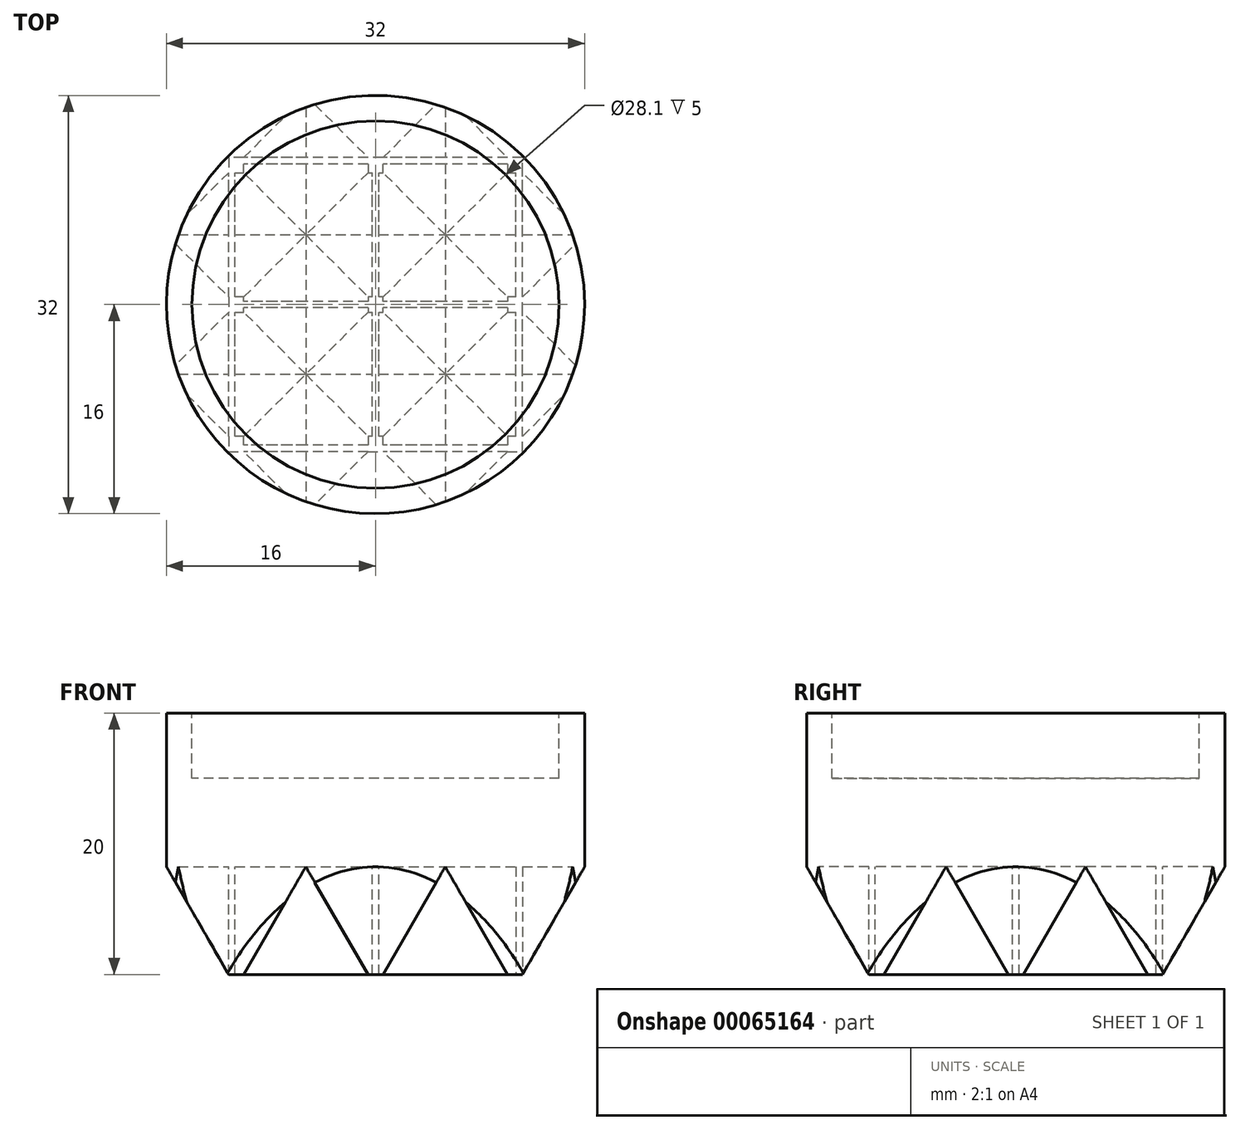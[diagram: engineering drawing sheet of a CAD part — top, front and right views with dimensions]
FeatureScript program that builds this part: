
annotation { "Feature Type Name" : "Feature", "Feature Type Description" : "" }
export const myFeature = defineFeature(function(context is Context, id is Id, definition is map)
    precondition{}
    {
        {
            var Q0;
            Q0=qCreatedBy(makeId("Top.planeOp"),FACE);
            var sketch = newSketch(context, id + "F0", { "sketchPlane" : qUnion([Q0])});
            skCircle(sketch, "E0", {"center": v(0, 0) * mm, "radius": 16 * mm});
            skSolve(sketch);
        }
        {
            var Q0;
            Q0 = qSketchRegion(id + "F0", true);
            extrude(context, id + "F1", {"entities" : qUnion([Q0]), "depth" : 20 * mm});
        }
        {
            var Q0;
            Q0=qCreatedBy(makeId("Front.planeOp"),FACE);
            var sketch = newSketch(context, id + "F2", { "sketchPlane" : qUnion([Q0])});
            skLineSegment(sketch, "E1", {"start": v(-21.33, -1) * mm, "end": v(-16, 8.24) * mm});
            skLineSegment(sketch, "E2", {"start": v(-16, 8.24) * mm, "end": v(-10.67, -1) * mm});
            skLineSegment(sketch, "E3", {"start": v(-10.67, -1) * mm, "end": v(-21.33, -1) * mm});
            skLineSegment(sketch, "E4.1.0.0", {"start": v(0, -1) * mm, "end": v(-10.67, -1) * mm});
            skLineSegment(sketch, "E4.1.0.1", {"start": v(-5.33, 8.24) * mm, "end": v(0, -1) * mm});
            skLineSegment(sketch, "E4.1.0.2", {"start": v(-10.67, -1) * mm, "end": v(-5.33, 8.24) * mm});
            skLineSegment(sketch, "E4.2.0.0", {"start": v(10.67, -1) * mm, "end": v(0, -1) * mm});
            skLineSegment(sketch, "E4.2.0.1", {"start": v(5.33, 8.24) * mm, "end": v(10.67, -1) * mm});
            skLineSegment(sketch, "E4.2.0.2", {"start": v(0, -1) * mm, "end": v(5.33, 8.24) * mm});
            skLineSegment(sketch, "E4.3.0.0", {"start": v(21.33, -1) * mm, "end": v(10.67, -1) * mm});
            skLineSegment(sketch, "E4.3.0.1", {"start": v(16, 8.24) * mm, "end": v(21.33, -1) * mm});
            skLineSegment(sketch, "E4.3.0.2", {"start": v(10.67, -1) * mm, "end": v(16, 8.24) * mm});
            skLineSegment(sketch, "E4.direction1", {"start": v(-21.33, -1) * mm, "end": v(-10.67, -1) * mm, "construction": true});
            skLineSegment(sketch, "E5", {"start": v(-16, 8.24) * mm, "end": v(16, 8.24) * mm, "construction": true});
            skPoint(sketch, "E6", {"position": v(0, 8.24) * mm});
            skSolve(sketch);
        }
        {
            var Q0;
            Q0 = qSketchRegion(id + "F2", true);
            extrude(context, id + "F3", {"entities" : qUnion([Q0]), "operationType" : NewBodyOperationType.REMOVE, "endBound" : BoundingType.SYMMETRIC, "oppositeDirection" : true, "depth" : 50 * mm});
        }
        {
            var Q0;
            Q0=qCreatedBy(makeId("Right.planeOp"),FACE);
            var sketch = newSketch(context, id + "F4", { "sketchPlane" : qUnion([Q0])});
            skLineSegment(sketch, "E7", {"start": v(-21.33, -1) * mm, "end": v(-16, 8.24) * mm});
            skLineSegment(sketch, "E8", {"start": v(-16, 8.24) * mm, "end": v(-10.67, -1) * mm});
            skLineSegment(sketch, "E9", {"start": v(-10.67, -1) * mm, "end": v(-21.33, -1) * mm});
            skLineSegment(sketch, "E10.1.0.0", {"start": v(0, -1) * mm, "end": v(-10.67, -1) * mm});
            skLineSegment(sketch, "E10.1.0.1", {"start": v(-5.33, 8.24) * mm, "end": v(0, -1) * mm});
            skLineSegment(sketch, "E10.1.0.2", {"start": v(-10.67, -1) * mm, "end": v(-5.33, 8.24) * mm});
            skLineSegment(sketch, "E10.2.0.0", {"start": v(10.67, -1) * mm, "end": v(0, -1) * mm});
            skLineSegment(sketch, "E10.2.0.1", {"start": v(5.33, 8.24) * mm, "end": v(10.67, -1) * mm});
            skLineSegment(sketch, "E10.2.0.2", {"start": v(0, -1) * mm, "end": v(5.33, 8.24) * mm});
            skLineSegment(sketch, "E10.3.0.0", {"start": v(21.33, -1) * mm, "end": v(10.67, -1) * mm});
            skLineSegment(sketch, "E10.3.0.1", {"start": v(16, 8.24) * mm, "end": v(21.33, -1) * mm});
            skLineSegment(sketch, "E10.3.0.2", {"start": v(10.67, -1) * mm, "end": v(16, 8.24) * mm});
            skLineSegment(sketch, "E10.direction1", {"start": v(-21.33, -1) * mm, "end": v(-10.67, -1) * mm, "construction": true});
            skLineSegment(sketch, "E11", {"start": v(-16, 8.24) * mm, "end": v(16, 8.24) * mm, "construction": true});
            skPoint(sketch, "E12", {"position": v(0, 8.24) * mm});
            skSolve(sketch);
        }
        {
            var Q0;
            Q0 = qSketchRegion(id + "F4", true);
            extrude(context, id + "F5", {"entities" : qUnion([Q0]), "operationType" : NewBodyOperationType.REMOVE, "endBound" : BoundingType.THROUGH_ALL, "oppositeDirection" : true, "depth" : 25 * mm, "hasSecondDirection" : true, "secondDirectionBound" : SecondDirectionBoundingType.THROUGH_ALL, "secondDirectionOppositeDirection" : false, "secondDirectionDepth" : 25 * mm});
        }
        {
            var Q0;
            Q0=makeQuery(id+"F1.opExtrude","CAP_FACE",FACE,{"disambiguationData":[OSD([sQuery(id+"F0.wireOp",EDGE,"E0")])],"isStart":false});
            var sketch = newSketch(context, id + "F6", { "sketchPlane" : qUnion([Q0])});
            skCircle(sketch, "E13", {"center": v(0, 0) * mm, "radius": 14.05 * mm});
            skSolve(sketch);
        }
        {
            var Q0;
            Q0 = qSketchRegion(id + "F6", true);
            extrude(context, id + "F7", {"entities" : qUnion([Q0]), "operationType" : NewBodyOperationType.REMOVE, "oppositeDirection" : true, "depth" : 5 * mm});
        }
        {
            var Q0;
            Q0=qCreatedBy(makeId("Top.planeOp"),FACE);
            var sketch = newSketch(context, id + "F8", { "sketchPlane" : qUnion([Q0])});
            skLineSegment(sketch, "E14.bottom", {"start": v(11.24, -11.24) * mm, "end": v(-11.24, -11.24) * mm});
            skLineSegment(sketch, "E14.top", {"start": v(10.74, -10.74) * mm, "end": v(0.25, -10.74) * mm});
            skLineSegment(sketch, "E14.left", {"start": v(11.24, -11.24) * mm, "end": v(11.24, -10.74) * mm});
            skLineSegment(sketch, "E14.right", {"start": v(-11.24, -11.24) * mm, "end": v(-11.24, -10.74) * mm});
            skLineSegment(sketch, "E15.MirrorCS", {"start": v(11.24, 11.24) * mm, "end": v(11.24, 10.74) * mm});
            skLineSegment(sketch, "E16.MirrorCS", {"start": v(-11.24, 11.24) * mm, "end": v(-11.24, 10.74) * mm});
            skLineSegment(sketch, "E17.MirrorCS", {"start": v(10.74, 10.74) * mm, "end": v(0.25, 10.74) * mm});
            skLineSegment(sketch, "E18.MirrorCS", {"start": v(11.24, 11.24) * mm, "end": v(-11.24, 11.24) * mm});
            skLineSegment(sketch, "E19.bottom", {"start": v(10.74, -0.25) * mm, "end": v(0.25, -0.25) * mm});
            skLineSegment(sketch, "E19.top", {"start": v(10.74, 0.25) * mm, "end": v(0.25, 0.25) * mm});
            skLineSegment(sketch, "E19.left", {"start": v(11.24, -0.25) * mm, "end": v(11.24, 0.25) * mm});
            skLineSegment(sketch, "E19.right", {"start": v(-11.24, -0.25) * mm, "end": v(-11.24, 0.25) * mm});
            skPoint(sketch, "E20", {"position": v(-11.24, 0) * mm});
            skLineSegment(sketch, "E21.left", {"start": v(-11.24, -10.74) * mm, "end": v(-11.24, 10.74) * mm});
            skLineSegment(sketch, "E21.right", {"start": v(-10.74, -10.74) * mm, "end": v(-10.74, -0.25) * mm});
            skLineSegment(sketch, "E22.left", {"start": v(11.24, -10.74) * mm, "end": v(11.24, 10.74) * mm});
            skLineSegment(sketch, "E22.right", {"start": v(10.74, -10.74) * mm, "end": v(10.74, -0.25) * mm});
            skLineSegment(sketch, "E23.left", {"start": v(-0.25, -10.74) * mm, "end": v(-0.25, -0.25) * mm});
            skLineSegment(sketch, "E23.right", {"start": v(0.25, -10.74) * mm, "end": v(0.25, -0.25) * mm});
            skPoint(sketch, "E24", {"position": v(0, -10.74) * mm});
            skLineSegment(sketch, "E25.trimOffspring", {"start": v(-0.25, 10.74) * mm, "end": v(-10.74, 10.74) * mm});
            skLineSegment(sketch, "E26.trimOffspring", {"start": v(-10.74, 0.25) * mm, "end": v(-10.74, 10.74) * mm});
            skLineSegment(sketch, "E27.trimOffspring", {"start": v(-0.25, 0.25) * mm, "end": v(-0.25, 10.74) * mm});
            skLineSegment(sketch, "E28.trimOffspring", {"start": v(-0.25, 0.25) * mm, "end": v(-10.74, 0.25) * mm});
            skLineSegment(sketch, "E29.trimOffspring", {"start": v(0.25, 0.25) * mm, "end": v(0.25, 10.74) * mm});
            skLineSegment(sketch, "E30.trimOffspring", {"start": v(-0.25, -0.25) * mm, "end": v(-10.74, -0.25) * mm});
            skLineSegment(sketch, "E31.trimOffspring", {"start": v(10.74, 0.25) * mm, "end": v(10.74, 10.74) * mm});
            skLineSegment(sketch, "E32.trimOffspring", {"start": v(-0.25, -10.74) * mm, "end": v(-10.74, -10.74) * mm});
            skSolve(sketch);
        }
        {
            var Q0;
            Q0 = qSketchRegion(id + "F8", true);
            extrude(context, id + "F9", {"entities" : qUnion([Q0]), "operationType" : NewBodyOperationType.ADD, "depth" : 10.92 * mm});
        }
    });
